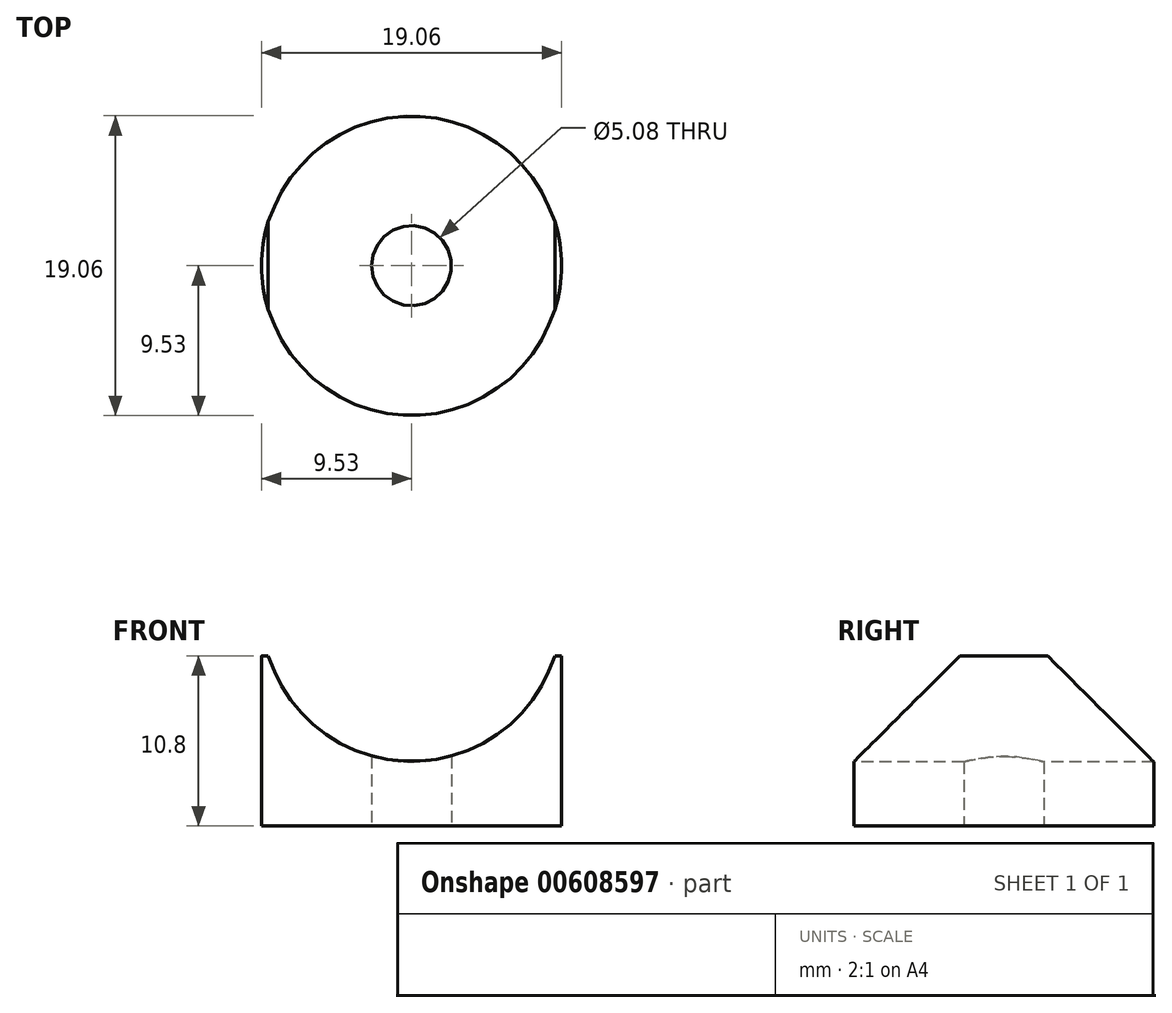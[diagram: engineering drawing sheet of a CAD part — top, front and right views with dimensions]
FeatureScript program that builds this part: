
annotation { "Feature Type Name" : "Feature", "Feature Type Description" : "" }
export const myFeature = defineFeature(function(context is Context, id is Id, definition is map)
    precondition{}
    {
        {
            var Q0;
            Q0=qCreatedBy(makeId("Top.planeOp"),FACE);
            var sketch = newSketch(context, id + "F0", { "sketchPlane" : qUnion([Q0])});
            skCircle(sketch, "E0", {"center": v(0, 0) * mm, "radius": 9.53 * mm});
            skCircle(sketch, "E1", {"center": v(0, 0) * mm, "radius": 2.54 * mm});
            skSolve(sketch);
        }
        {
            var Q0;
            Q0=makeQuery(id+"F0.imprint","IMPRINT",FACE,{"disambiguationData":[TD([[makeQuery(id+"F0.imprint","IMPRINT",EDGE,{"derivedFrom":sQuery(id+"F0.wireOp",EDGE,"E0")}),1.0]])]});
            extrude(context, id + "F1", {"entities" : qUnion([Q0]), "depth" : 10.8 * mm, "offsetDistance" : 25.4 * mm});
        }
        {
            var Q0;
            Q0=qCreatedBy(makeId("Front.planeOp"),FACE);
            var sketch = newSketch(context, id + "F2", { "sketchPlane" : qUnion([Q0])});
            skCircle(sketch, "E2", {"center": v(0, 13.59) * mm, "radius": 9.53 * mm});
            skSolve(sketch);
        }
        {
            var Q0;
            Q0=makeQuery(id+"F2.imprint","IMPRINT",FACE,{"disambiguationData":[TD([[makeQuery(id+"F2.imprint","IMPRINT",EDGE,{"derivedFrom":sQuery(id+"F2.wireOp",EDGE,"E2")}),1.0]])]});
            extrude(context, id + "F3", {"entities" : qUnion([Q0]), "operationType" : NewBodyOperationType.REMOVE, "endBound" : BoundingType.SYMMETRIC, "oppositeDirection" : true, "depth" : 25.4 * mm, "offsetDistance" : 25.4 * mm});
        }
    });
